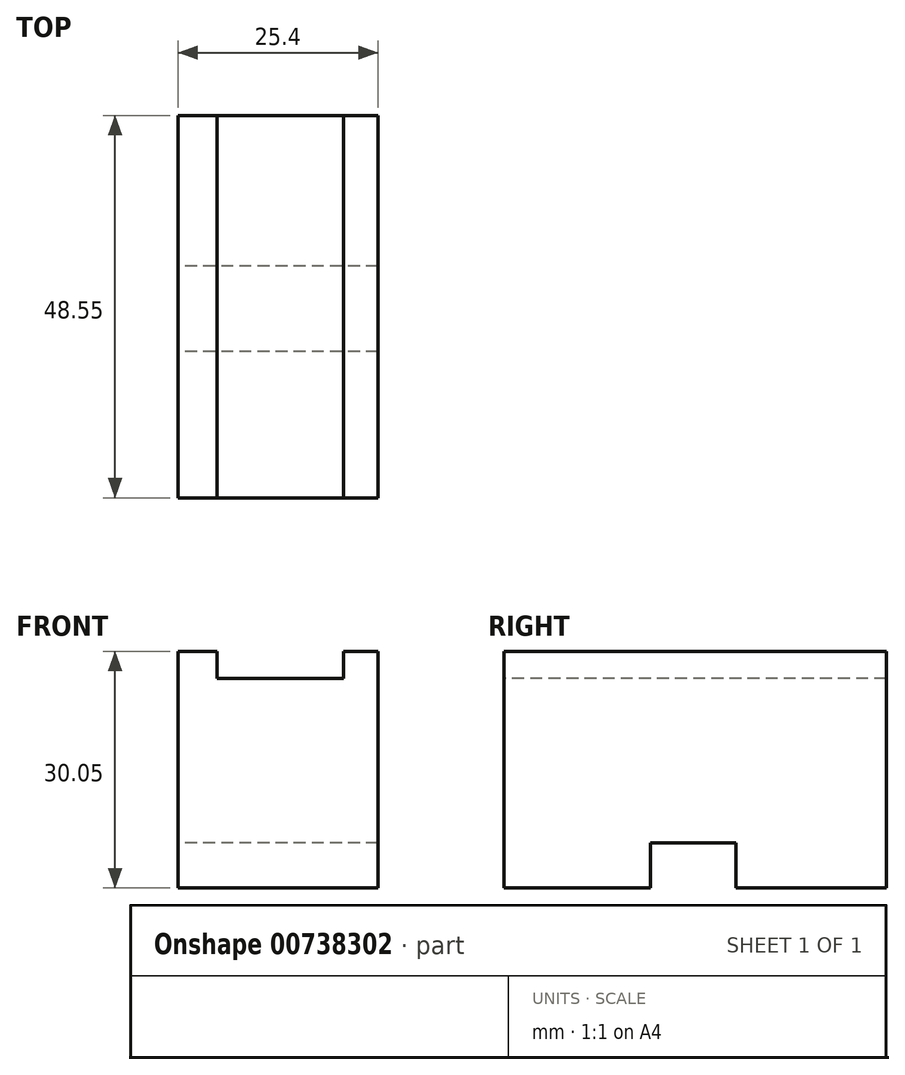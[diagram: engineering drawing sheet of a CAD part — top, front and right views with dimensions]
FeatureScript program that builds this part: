
annotation { "Feature Type Name" : "Feature", "Feature Type Description" : "" }
export const myFeature = defineFeature(function(context is Context, id is Id, definition is map)
    precondition{}
    {
        {
            var Q0;
            Q0=qCreatedBy(makeId("Right.planeOp"),FACE);
            var sketch = newSketch(context, id + "F0", { "sketchPlane" : qUnion([Q0])});
            skLineSegment(sketch, "E0", {"start": v(0, 0) * mm, "end": v(48.55, 0) * mm});
            skLineSegment(sketch, "E1", {"start": v(48.55, 0) * mm, "end": v(48.55, 30.05) * mm});
            skLineSegment(sketch, "E2", {"start": v(48.55, 30.05) * mm, "end": v(0, 30.05) * mm});
            skLineSegment(sketch, "E3", {"start": v(0, 30.05) * mm, "end": v(0, 0) * mm});
            skSolve(sketch);
        }
        {
            var Q0;
            Q0=makeQuery(id+"F0.imprint","IMPRINT",FACE,{"disambiguationData":[TD([[makeQuery(id+"F0.imprint","IMPRINT",EDGE,{"derivedFrom":sQuery(id+"F0.wireOp",EDGE,"E0")}),1.0]])]});
            extrude(context, id + "F1", {"entities" : qUnion([Q0]), "depth" : 25.4 * mm, "offsetDistance" : 25.4 * mm});
        }
        {
            var Q0;
            Q0=makeQuery(id+"F1.opExtrude","SWEPT_FACE",FACE,{"disambiguationData":[OSD([sQuery(id+"F0.wireOp",EDGE,"E3")])]});
            var sketch = newSketch(context, id + "F2", { "sketchPlane" : qUnion([Q0])});
            skLineSegment(sketch, "E4", {"start": v(4.93, 30.05) * mm, "end": v(4.93, 26.64) * mm});
            skLineSegment(sketch, "E5", {"start": v(4.93, 26.64) * mm, "end": v(21, 26.64) * mm});
            skLineSegment(sketch, "E6", {"start": v(21, 26.64) * mm, "end": v(21, 30.05) * mm});
            skSolve(sketch);
        }
        {
            var Q0;
            {var subQ0=sQuery(id+"F2.wireOp",EDGE,"E4");Q0=makeQuery(id+"F2.imprint","IMPRINT",FACE,{"disambiguationData":[TD([[makeQuery(id+"F2.imprint","IMPRINT",EDGE,{"derivedFrom":subQ0}),1.0]])]});}
            extrude(context, id + "F3", {"entities" : qUnion([Q0]), "operationType" : NewBodyOperationType.REMOVE, "oppositeDirection" : true, "depth" : 50.8 * mm, "offsetDistance" : 25.4 * mm});
        }
        {
            var Q0;
            Q0=makeQuery(id+"F1.opExtrude","CAP_FACE",FACE,{"disambiguationData":[OSD([sQuery(id+"F0.wireOp",EDGE,"E0"),sQuery(id+"F0.wireOp",EDGE,"E1"),sQuery(id+"F0.wireOp",EDGE,"E2"),sQuery(id+"F0.wireOp",EDGE,"E3")])],"isStart":true});
            var sketch = newSketch(context, id + "F4", { "sketchPlane" : qUnion([Q0])});
            skLineSegment(sketch, "E7", {"start": v(-29.45, 0) * mm, "end": v(-29.45, 5.73) * mm});
            skLineSegment(sketch, "E8", {"start": v(-29.45, 5.73) * mm, "end": v(-18.6, 5.73) * mm});
            skLineSegment(sketch, "E9", {"start": v(-18.6, 5.73) * mm, "end": v(-18.6, 0) * mm});
            skSolve(sketch);
        }
        {
            var Q0;
            {var subQ0=sQuery(id+"F4.wireOp",EDGE,"E7");Q0=makeQuery(id+"F4.imprint","IMPRINT",FACE,{"disambiguationData":[TD([[makeQuery(id+"F4.imprint","IMPRINT",EDGE,{"derivedFrom":subQ0}),-1.0]])]});}
            extrude(context, id + "F5", {"entities" : qUnion([Q0]), "operationType" : NewBodyOperationType.REMOVE, "oppositeDirection" : true, "depth" : 50.8 * mm, "offsetDistance" : 25.4 * mm});
        }
    });
